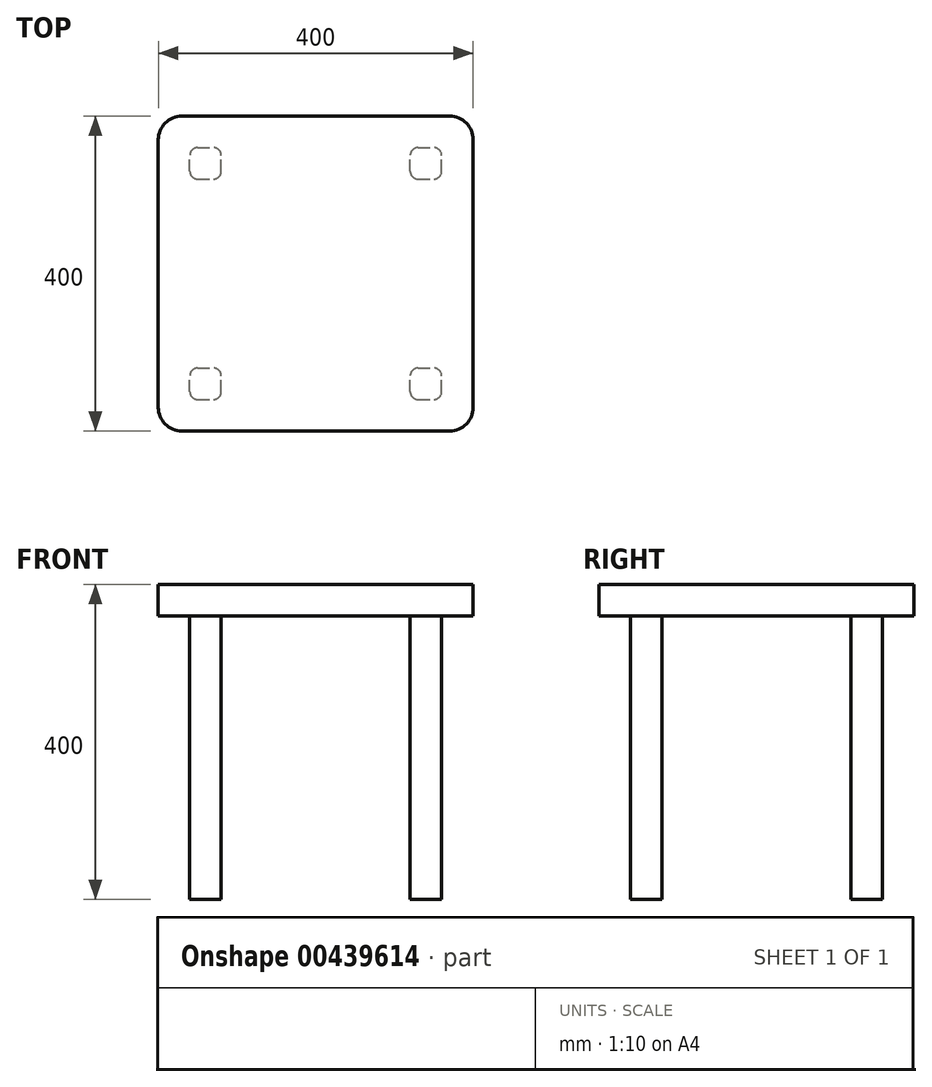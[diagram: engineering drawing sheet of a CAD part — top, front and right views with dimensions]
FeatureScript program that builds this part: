
annotation { "Feature Type Name" : "Feature", "Feature Type Description" : "" }
export const myFeature = defineFeature(function(context is Context, id is Id, definition is map)
    precondition{}
    {
        {
            var Q0;
            Q0=qCreatedBy(makeId("Top.planeOp"),FACE);
            var sketch = newSketch(context, id + "F0", { "sketchPlane" : qUnion([Q0])});
            skLineSegment(sketch, "E0.bottom", {"start": v(-161.92, 137.01) * mm, "end": v(178.08, 137.01) * mm});
            skLineSegment(sketch, "E0.top", {"start": v(-161.92, -262.99) * mm, "end": v(178.08, -262.99) * mm});
            skLineSegment(sketch, "E0.left", {"start": v(-191.92, 107.01) * mm, "end": v(-191.92, -232.99) * mm});
            skLineSegment(sketch, "E0.right", {"start": v(208.08, 107.01) * mm, "end": v(208.08, -232.99) * mm});
            skPoint(sketch, "E1.visualSharp", {"position": v(-191.92, 137.01) * mm});
            skArc(sketch, "E1.filletArc", {"start": v(-161.92, 137.01) * mm, "mid": v(-183.14, 128.23) * mm, "end": v(-191.92, 107.01) * mm});
            skPoint(sketch, "E2.visualSharp", {"position": v(208.08, 137.01) * mm});
            skArc(sketch, "E2.filletArc", {"start": v(208.08, 107.01) * mm, "mid": v(199.3, 128.23) * mm, "end": v(178.08, 137.01) * mm});
            skPoint(sketch, "E3.visualSharp", {"position": v(208.08, -262.99) * mm});
            skArc(sketch, "E3.filletArc", {"start": v(178.08, -262.99) * mm, "mid": v(199.3, -254.2) * mm, "end": v(208.08, -232.99) * mm});
            skPoint(sketch, "E4.visualSharp", {"position": v(-191.92, -262.99) * mm});
            skArc(sketch, "E4.filletArc", {"start": v(-191.92, -232.99) * mm, "mid": v(-183.14, -254.2) * mm, "end": v(-161.92, -262.99) * mm});
            skSolve(sketch);
        }
        {
            var Q0;
            Q0=makeQuery(id+"F0.imprint","IMPRINT",FACE,{"disambiguationData":[TD([[makeQuery(id+"F0.imprint","IMPRINT",EDGE,{"derivedFrom":sQuery(id+"F0.wireOp",EDGE,"E0.bottom")}),-1.0]])]});
            extrude(context, id + "F1", {"entities" : qUnion([Q0]), "depth" : 40 * mm});
        }
        {
            var Q0;
            Q0=makeQuery(id+"F1.opExtrude","CAP_FACE",FACE,{"disambiguationData":[OSD([sQuery(id+"F0.wireOp",EDGE,"E0.bottom"),sQuery(id+"F0.wireOp",EDGE,"E0.top"),sQuery(id+"F0.wireOp",EDGE,"E0.left"),sQuery(id+"F0.wireOp",EDGE,"E0.right"),sQuery(id+"F0.wireOp",EDGE,"E1.filletArc"),sQuery(id+"F0.wireOp",EDGE,"E2.filletArc"),sQuery(id+"F0.wireOp",EDGE,"E3.filletArc"),sQuery(id+"F0.wireOp",EDGE,"E4.filletArc")])],"isStart":true});
            var sketch = newSketch(context, id + "F2", { "sketchPlane" : qUnion([Q0])});
            skLineSegment(sketch, "E5.bottom", {"start": v(-141.92, -57.01) * mm, "end": v(-121.92, -57.01) * mm});
            skLineSegment(sketch, "E5.top", {"start": v(-141.92, -97.01) * mm, "end": v(-121.92, -97.01) * mm});
            skLineSegment(sketch, "E5.left", {"start": v(-151.92, -67.01) * mm, "end": v(-151.92, -87.01) * mm});
            skLineSegment(sketch, "E5.right", {"start": v(-111.92, -67.01) * mm, "end": v(-111.92, -87.01) * mm});
            skPoint(sketch, "E6.visualSharp", {"position": v(-151.92, -57.01) * mm});
            skArc(sketch, "E6.filletArc", {"start": v(-141.92, -57.01) * mm, "mid": v(-149, -59.94) * mm, "end": v(-151.92, -67.01) * mm});
            skPoint(sketch, "E7.visualSharp", {"position": v(-111.92, -57.01) * mm});
            skArc(sketch, "E7.filletArc", {"start": v(-111.92, -67.01) * mm, "mid": v(-114.85, -59.94) * mm, "end": v(-121.92, -57.01) * mm});
            skPoint(sketch, "E8.visualSharp", {"position": v(-111.92, -97.01) * mm});
            skArc(sketch, "E8.filletArc", {"start": v(-121.92, -97.01) * mm, "mid": v(-114.85, -94.09) * mm, "end": v(-111.92, -87.01) * mm});
            skPoint(sketch, "E9.visualSharp", {"position": v(-151.92, -97.01) * mm});
            skArc(sketch, "E9.filletArc", {"start": v(-151.92, -87.01) * mm, "mid": v(-149, -94.09) * mm, "end": v(-141.92, -97.01) * mm});
            skSolve(sketch);
        }
        {
            var Q0;
            Q0=makeQuery(id+"F2.imprint","IMPRINT",FACE,{"disambiguationData":[TD([[makeQuery(id+"F2.imprint","IMPRINT",EDGE,{"derivedFrom":sQuery(id+"F2.wireOp",EDGE,"E5.bottom")}),1.0]])]});
            var sketch = newSketch(context, id + "F3", { "sketchPlane" : qUnion([Q0])});
            skLineSegment(sketch, "E10.bottom", {"start": v(-141.92, 222.99) * mm, "end": v(-121.92, 222.99) * mm});
            skLineSegment(sketch, "E10.top", {"start": v(-141.92, 182.99) * mm, "end": v(-121.92, 182.99) * mm});
            skLineSegment(sketch, "E10.left", {"start": v(-151.92, 212.99) * mm, "end": v(-151.92, 192.99) * mm});
            skLineSegment(sketch, "E10.right", {"start": v(-111.92, 212.99) * mm, "end": v(-111.92, 192.99) * mm});
            skPoint(sketch, "E11.visualSharp", {"position": v(-151.92, 222.99) * mm});
            skArc(sketch, "E11.filletArc", {"start": v(-141.92, 222.99) * mm, "mid": v(-149, 220.06) * mm, "end": v(-151.92, 212.99) * mm});
            skPoint(sketch, "E12.visualSharp", {"position": v(-111.92, 222.99) * mm});
            skArc(sketch, "E12.filletArc", {"start": v(-111.92, 212.99) * mm, "mid": v(-114.85, 220.06) * mm, "end": v(-121.92, 222.99) * mm});
            skPoint(sketch, "E13.visualSharp", {"position": v(-111.92, 182.99) * mm});
            skArc(sketch, "E13.filletArc", {"start": v(-121.92, 182.99) * mm, "mid": v(-114.85, 185.91) * mm, "end": v(-111.92, 192.99) * mm});
            skPoint(sketch, "E14.visualSharp", {"position": v(-151.92, 182.99) * mm});
            skArc(sketch, "E14.filletArc", {"start": v(-151.92, 192.99) * mm, "mid": v(-149, 185.91) * mm, "end": v(-141.92, 182.99) * mm});
            skSolve(sketch);
        }
        {
            var Q0;
            Q0=qCreatedBy(makeId("Top.planeOp"),FACE);
            var sketch = newSketch(context, id + "F4", { "sketchPlane" : qUnion([Q0])});
            skLineSegment(sketch, "E15.bottom", {"start": v(138.08, -222.99) * mm, "end": v(158.08, -222.99) * mm});
            skLineSegment(sketch, "E15.top", {"start": v(138.08, -182.99) * mm, "end": v(158.08, -182.99) * mm});
            skLineSegment(sketch, "E15.left", {"start": v(128.08, -212.99) * mm, "end": v(128.08, -192.99) * mm});
            skLineSegment(sketch, "E15.right", {"start": v(168.08, -212.99) * mm, "end": v(168.08, -192.99) * mm});
            skPoint(sketch, "E16.visualSharp", {"position": v(128.08, -222.99) * mm});
            skArc(sketch, "E16.filletArc", {"start": v(128.08, -212.99) * mm, "mid": v(131, -220.06) * mm, "end": v(138.08, -222.99) * mm});
            skPoint(sketch, "E17.visualSharp", {"position": v(168.08, -222.99) * mm});
            skArc(sketch, "E17.filletArc", {"start": v(158.08, -222.99) * mm, "mid": v(165.15, -220.06) * mm, "end": v(168.08, -212.99) * mm});
            skPoint(sketch, "E18.visualSharp", {"position": v(168.08, -182.99) * mm});
            skArc(sketch, "E18.filletArc", {"start": v(168.08, -192.99) * mm, "mid": v(165.15, -185.91) * mm, "end": v(158.08, -182.99) * mm});
            skPoint(sketch, "E19.visualSharp", {"position": v(128.08, -182.99) * mm});
            skArc(sketch, "E19.filletArc", {"start": v(138.08, -182.99) * mm, "mid": v(131, -185.91) * mm, "end": v(128.08, -192.99) * mm});
            skSolve(sketch);
        }
        {
            var Q0;
            Q0=makeQuery(id+"F2.imprint","IMPRINT",FACE,{"disambiguationData":[TD([[makeQuery(id+"F2.imprint","IMPRINT",EDGE,{"derivedFrom":sQuery(id+"F2.wireOp",EDGE,"E5.bottom")}),1.0]])]});
            var sketch = newSketch(context, id + "F5", { "sketchPlane" : qUnion([Q0])});
            skLineSegment(sketch, "E20.bottom", {"start": v(138.08, -57.01) * mm, "end": v(158.08, -57.01) * mm});
            skLineSegment(sketch, "E20.top", {"start": v(138.08, -97.01) * mm, "end": v(158.08, -97.01) * mm});
            skLineSegment(sketch, "E20.left", {"start": v(128.08, -67.01) * mm, "end": v(128.08, -87.01) * mm});
            skLineSegment(sketch, "E20.right", {"start": v(168.08, -67.01) * mm, "end": v(168.08, -87.01) * mm});
            skPoint(sketch, "E21.visualSharp", {"position": v(128.08, -57.01) * mm});
            skArc(sketch, "E21.filletArc", {"start": v(138.08, -57.01) * mm, "mid": v(131, -59.94) * mm, "end": v(128.08, -67.01) * mm});
            skPoint(sketch, "E22.visualSharp", {"position": v(168.08, -57.01) * mm});
            skArc(sketch, "E22.filletArc", {"start": v(168.08, -67.01) * mm, "mid": v(165.15, -59.94) * mm, "end": v(158.08, -57.01) * mm});
            skPoint(sketch, "E23.visualSharp", {"position": v(168.08, -97.01) * mm});
            skArc(sketch, "E23.filletArc", {"start": v(158.08, -97.01) * mm, "mid": v(165.15, -94.09) * mm, "end": v(168.08, -87.01) * mm});
            skPoint(sketch, "E24.visualSharp", {"position": v(128.08, -97.01) * mm});
            skArc(sketch, "E24.filletArc", {"start": v(128.08, -87.01) * mm, "mid": v(131, -94.09) * mm, "end": v(138.08, -97.01) * mm});
            skSolve(sketch);
        }
        {
            var Q0;
            Q0=makeQuery(id+"F2.imprint","IMPRINT",FACE,{"disambiguationData":[TD([[makeQuery(id+"F2.imprint","IMPRINT",EDGE,{"derivedFrom":sQuery(id+"F2.wireOp",EDGE,"E5.bottom")}),-1.0]])]});
            extrude(context, id + "F6", {"entities" : qUnion([Q0]), "operationType" : NewBodyOperationType.ADD, "depth" : 360 * mm});
        }
        {
            var Q0;
            Q0=makeQuery(id+"F5.imprint","IMPRINT",FACE,{"disambiguationData":[TD([[makeQuery(id+"F5.imprint","IMPRINT",EDGE,{"derivedFrom":sQuery(id+"F5.wireOp",EDGE,"E20.bottom")}),-1.0]])]});
            extrude(context, id + "F7", {"entities" : qUnion([Q0]), "operationType" : NewBodyOperationType.ADD, "depth" : 360 * mm});
        }
        {
            var Q0;
            Q0=makeQuery(id+"F3.imprint","IMPRINT",FACE,{"disambiguationData":[TD([[makeQuery(id+"F3.imprint","IMPRINT",EDGE,{"derivedFrom":sQuery(id+"F3.wireOp",EDGE,"E10.bottom")}),-1.0]])]});
            extrude(context, id + "F8", {"entities" : qUnion([Q0]), "operationType" : NewBodyOperationType.ADD, "depth" : 360 * mm});
        }
        {
            var Q0;
            Q0=makeQuery(id+"F4.imprint","IMPRINT",FACE,{"disambiguationData":[TD([[makeQuery(id+"F4.imprint","IMPRINT",EDGE,{"derivedFrom":sQuery(id+"F4.wireOp",EDGE,"E15.bottom")}),1.0]])]});
            extrude(context, id + "F9", {"entities" : qUnion([Q0]), "operationType" : NewBodyOperationType.ADD, "oppositeDirection" : true, "depth" : 360 * mm});
        }
    });
